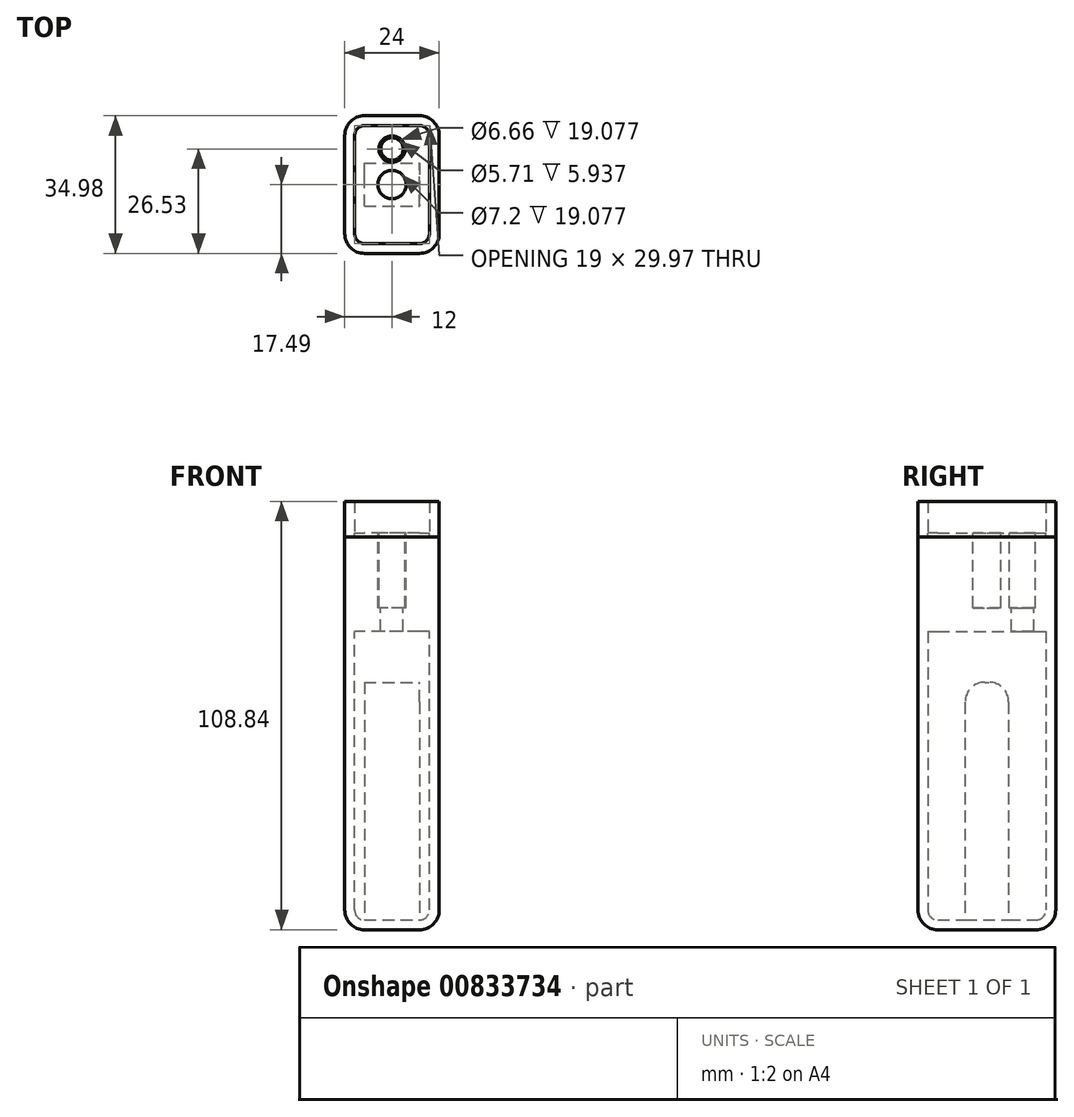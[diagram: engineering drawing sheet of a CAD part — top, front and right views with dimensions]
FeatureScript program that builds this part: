
annotation { "Feature Type Name" : "Feature", "Feature Type Description" : "" }
export const myFeature = defineFeature(function(context is Context, id is Id, definition is map)
    precondition{}
    {
        {
            var Q0;
            Q0=qCreatedBy(makeId("Top.planeOp"),FACE);
            var sketch = newSketch(context, id + "F0", { "sketchPlane" : qUnion([Q0])});
            skLineSegment(sketch, "E0.bottom", {"start": v(12, -17.49) * mm, "end": v(-12, -17.49) * mm});
            skLineSegment(sketch, "E0.top", {"start": v(12, 17.49) * mm, "end": v(-12, 17.49) * mm});
            skLineSegment(sketch, "E0.left", {"start": v(12, -17.49) * mm, "end": v(12, 17.49) * mm});
            skLineSegment(sketch, "E0.right", {"start": v(-12, -17.49) * mm, "end": v(-12, 17.49) * mm});
            skPoint(sketch, "E0.middle", {"position": v(0, 0) * mm});
            skSolve(sketch);
        }
        {
            var Q0;
            Q0 = qSketchRegion(id + "F0", true);
            extrude(context, id + "F1", {"entities" : qUnion([Q0]), "depth" : 74.84 * mm, "offsetDistance" : 25 * mm});
        }
        {
            var Q0;
            Q0=makeQuery(id+"F1.opExtrude","SWEPT_EDGE",EDGE,{"disambiguationData":[OSD([sQuery(id+"F0.wireOp",EDGE,"E0.bottom"),sQuery(id+"F0.wireOp",EDGE,"E0.left")])]});
            var Q1;
            Q1=makeQuery(id+"F1.opExtrude","SWEPT_EDGE",EDGE,{"disambiguationData":[OSD([sQuery(id+"F0.wireOp",EDGE,"E0.top"),sQuery(id+"F0.wireOp",EDGE,"E0.left")])]});
            var Q2;
            Q2=makeQuery(id+"F1.opExtrude","SWEPT_EDGE",EDGE,{"disambiguationData":[OSD([sQuery(id+"F0.wireOp",EDGE,"E0.top"),sQuery(id+"F0.wireOp",EDGE,"E0.right")])]});
            var Q3;
            Q3=makeQuery(id+"F1.opExtrude","SWEPT_EDGE",EDGE,{"disambiguationData":[OSD([sQuery(id+"F0.wireOp",EDGE,"E0.bottom"),sQuery(id+"F0.wireOp",EDGE,"E0.right")])]});
            var Q4;
            Q4=makeQuery(id+"F1.opExtrude","CAP_EDGE",EDGE,{"disambiguationData":[OSD([sQuery(id+"F0.wireOp",EDGE,"E0.right")])],"isStart":true});
            var Q5;
            Q5=makeQuery(id+"F1.opExtrude","CAP_EDGE",EDGE,{"disambiguationData":[OSD([sQuery(id+"F0.wireOp",EDGE,"E0.left")])],"isStart":true});
            var Q6;
            Q6=makeQuery(id+"F1.opExtrude","CAP_EDGE",EDGE,{"disambiguationData":[OSD([sQuery(id+"F0.wireOp",EDGE,"E0.top")])],"isStart":true});
            var Q7;
            Q7=makeQuery(id+"F1.opExtrude","CAP_EDGE",EDGE,{"disambiguationData":[OSD([sQuery(id+"F0.wireOp",EDGE,"E0.bottom")])],"isStart":true});
            fillet(context, id + "F2", {"entities" : qUnion([Q0, Q1, Q2, Q3, Q4, Q5, Q6, Q7]), "radius" : 5 * mm, "tangentPropagation" : true, "allowEdgeOverflow" : false});
        }
        {
            var Q0;
            Q0=makeQuery(id+"F1.opExtrude","CAP_FACE",FACE,{"disambiguationData":[OSD([sQuery(id+"F0.wireOp",EDGE,"E0.bottom"),sQuery(id+"F0.wireOp",EDGE,"E0.top"),sQuery(id+"F0.wireOp",EDGE,"E0.left"),sQuery(id+"F0.wireOp",EDGE,"E0.right")])],"isStart":false});
            shell(context, id + "F3", {"entities" : qUnion([Q0]), "thickness" : 2.5 * mm});
        }
        {
            var Q0;
            Q0=makeQuery(id+"F3.opShell","OFFSET_FACE",FACE,{"disambiguationData":[OSD([sQuery(id+"F0.wireOp",EDGE,"E0.bottom"),sQuery(id+"F0.wireOp",EDGE,"E0.top"),sQuery(id+"F0.wireOp",EDGE,"E0.left"),sQuery(id+"F0.wireOp",EDGE,"E0.right")])]});
            var sketch = newSketch(context, id + "F4", { "sketchPlane" : qUnion([Q0])});
            skLineSegment(sketch, "E1.bottom", {"start": v(-7, 5.52) * mm, "end": v(7, 5.52) * mm});
            skLineSegment(sketch, "E1.top", {"start": v(-7, -5.52) * mm, "end": v(7, -5.52) * mm});
            skLineSegment(sketch, "E1.left", {"start": v(-7, 5.52) * mm, "end": v(-7, -5.52) * mm});
            skLineSegment(sketch, "E1.right", {"start": v(7, 5.52) * mm, "end": v(7, -5.52) * mm});
            skPoint(sketch, "E1.middle", {"position": v(0, 0) * mm});
            skSolve(sketch);
        }
        {
            var Q0;
            Q0 = qSketchRegion(id + "F4", true);
            extrude(context, id + "F5", {"entities" : qUnion([Q0]), "operationType" : NewBodyOperationType.ADD, "depth" : 60.38 * mm, "offsetDistance" : 25 * mm});
        }
        {
            var Q0;
            Q0=makeQuery(id+"F5.opExtrude","CAP_EDGE",EDGE,{"disambiguationData":[OSD([sQuery(id+"F4.wireOp",EDGE,"E1.top")])],"isStart":false});
            var Q1;
            Q1=makeQuery(id+"F5.opExtrude","CAP_EDGE",EDGE,{"disambiguationData":[OSD([sQuery(id+"F4.wireOp",EDGE,"E1.bottom")])],"isStart":false});
            fillet(context, id + "F6", {"entities" : qUnion([Q0, Q1]), "radius" : 5 * mm, "tangentPropagation" : true, "allowEdgeOverflow" : false});
        }
        {
            var Q0;
            Q0=makeQuery(id+"F1.opExtrude","CAP_FACE",FACE,{"disambiguationData":[OSD([sQuery(id+"F0.wireOp",EDGE,"E0.bottom"),sQuery(id+"F0.wireOp",EDGE,"E0.top"),sQuery(id+"F0.wireOp",EDGE,"E0.left"),sQuery(id+"F0.wireOp",EDGE,"E0.right")])],"isStart":false});
            extrude(context, id + "F7", {"entities" : qUnion([Q0]), "operationType" : NewBodyOperationType.ADD, "depth" : 25 * mm, "offsetDistance" : 25 * mm});
        }
        {
            var Q0;
            Q0=makeQuery(id+"F7.opExtrude","CAP_FACE",FACE,{"disambiguationData":[OSD([sQuery(id+"F0.wireOp",EDGE,"E0.bottom"),sQuery(id+"F0.wireOp",EDGE,"E0.top"),sQuery(id+"F0.wireOp",EDGE,"E0.left"),sQuery(id+"F0.wireOp",EDGE,"E0.right")])],"isStart":false});
            var sketch = newSketch(context, id + "F8", { "sketchPlane" : qUnion([Q0])});
            skLineSegment(sketch, "E2.bottom", {"start": v(-10.53, 16.02) * mm, "end": v(10.53, 16.02) * mm});
            skLineSegment(sketch, "E2.top", {"start": v(-10.53, -16.02) * mm, "end": v(10.53, -16.02) * mm});
            skLineSegment(sketch, "E2.left", {"start": v(-10.53, 16.02) * mm, "end": v(-10.53, -16.02) * mm});
            skLineSegment(sketch, "E2.right", {"start": v(10.53, 16.02) * mm, "end": v(10.53, -16.02) * mm});
            skPoint(sketch, "E2.middle", {"position": v(0, 0) * mm});
            skSolve(sketch);
        }
        {
            var Q0;
            {var subQ3=sQuery(id+"F0.wireOp",EDGE,"E0.bottom");Q0=makeQuery(id+"F8.imprint","IMPRINT",FACE,{"disambiguationData":[TD([[makeQuery(id+"F8.imprint","IMPRINT",EDGE,{"derivedFrom":makeQuery(id+"F7.opExtrude","CAP_EDGE",EDGE,{"disambiguationData":[OSD([subQ3]),TDD([makeQuery(id+"F3.opShell","OFFSET_EDGE",EDGE,{"disambiguationData":[OSD([subQ3]),TDD([makeQuery(id+"F1.opExtrude","CAP_EDGE",EDGE,{"disambiguationData":[OSD([subQ3])],"isStart":false})])]})])],"isStart":false})}),-1.0]])]});}
            extrude(context, id + "F9", {"entities" : qUnion([Q0]), "oppositeDirection" : true, "depth" : 24 * mm, "offsetDistance" : 25 * mm});
        }
        {
            var Q0;
            Q0=makeQuery(id+"F9.opExtrude","CAP_FACE",FACE,{"disambiguationData":[OSD([sQuery(id+"F0.wireOp",EDGE,"E0.bottom"),sQuery(id+"F0.wireOp",EDGE,"E0.top"),sQuery(id+"F0.wireOp",EDGE,"E0.left"),sQuery(id+"F0.wireOp",EDGE,"E0.right")])],"isStart":true});
            var sketch = newSketch(context, id + "F10", { "sketchPlane" : qUnion([Q0])});
            skCircle(sketch, "E3", {"center": v(0, 9.04) * mm, "radius": 3.33 * mm});
            skPoint(sketch, "E3.centerSnap0", {"position": v(0, 14.99) * mm});
            skCircle(sketch, "E4", {"center": v(0, 0) * mm, "radius": 3.6 * mm});
            skSolve(sketch);
        }
        {
            var Q0;
            Q0 = qSketchRegion(id + "F10", true);
            extrude(context, id + "F11", {"entities" : qUnion([Q0]), "operationType" : NewBodyOperationType.REMOVE, "oppositeDirection" : true, "depth" : 18.07 * mm, "offsetDistance" : 25 * mm});
        }
        {
            var Q0;
            Q0=makeQuery(id+"F11.boolean.opBoolean","COPY",FACE,{"derivedFrom":makeQuery(id+"F11.opExtrude","CAP_FACE",FACE,{"disambiguationData":[OSD([sQuery(id+"F10.wireOp",EDGE,"E3")])],"isStart":false})});
            var sketch = newSketch(context, id + "F12", { "sketchPlane" : qUnion([Q0])});
            skCircle(sketch, "E5", {"center": v(0, 9.04) * mm, "radius": 2.86 * mm});
            skSolve(sketch);
        }
        {
            var Q0;
            Q0 = qSketchRegion(id + "F12", true);
            extrude(context, id + "F13", {"entities" : qUnion([Q0]), "operationType" : NewBodyOperationType.REMOVE, "oppositeDirection" : true, "depth" : 25 * mm, "offsetDistance" : 25 * mm});
        }
        {
            var Q0;
            Q0=makeQuery(id+"F9.opExtrude","CAP_FACE",FACE,{"disambiguationData":[OSD([sQuery(id+"F0.wireOp",EDGE,"E0.bottom"),sQuery(id+"F0.wireOp",EDGE,"E0.top"),sQuery(id+"F0.wireOp",EDGE,"E0.left"),sQuery(id+"F0.wireOp",EDGE,"E0.right")])],"isStart":true});
            extrude(context, id + "F14", {"entities" : qUnion([Q0]), "operationType" : NewBodyOperationType.ADD, "depth" : 1 * mm, "offsetDistance" : 25 * mm});
        }
        {
            var Q0;
            Q0=makeQuery(id+"F7.opExtrude","CAP_FACE",FACE,{"disambiguationData":[OSD([sQuery(id+"F0.wireOp",EDGE,"E0.bottom"),sQuery(id+"F0.wireOp",EDGE,"E0.top"),sQuery(id+"F0.wireOp",EDGE,"E0.left"),sQuery(id+"F0.wireOp",EDGE,"E0.right")])],"isStart":false});
            extrude(context, id + "F15", {"entities" : qUnion([Q0]), "depth" : 9 * mm, "offsetDistance" : 25 * mm});
        }
    });
